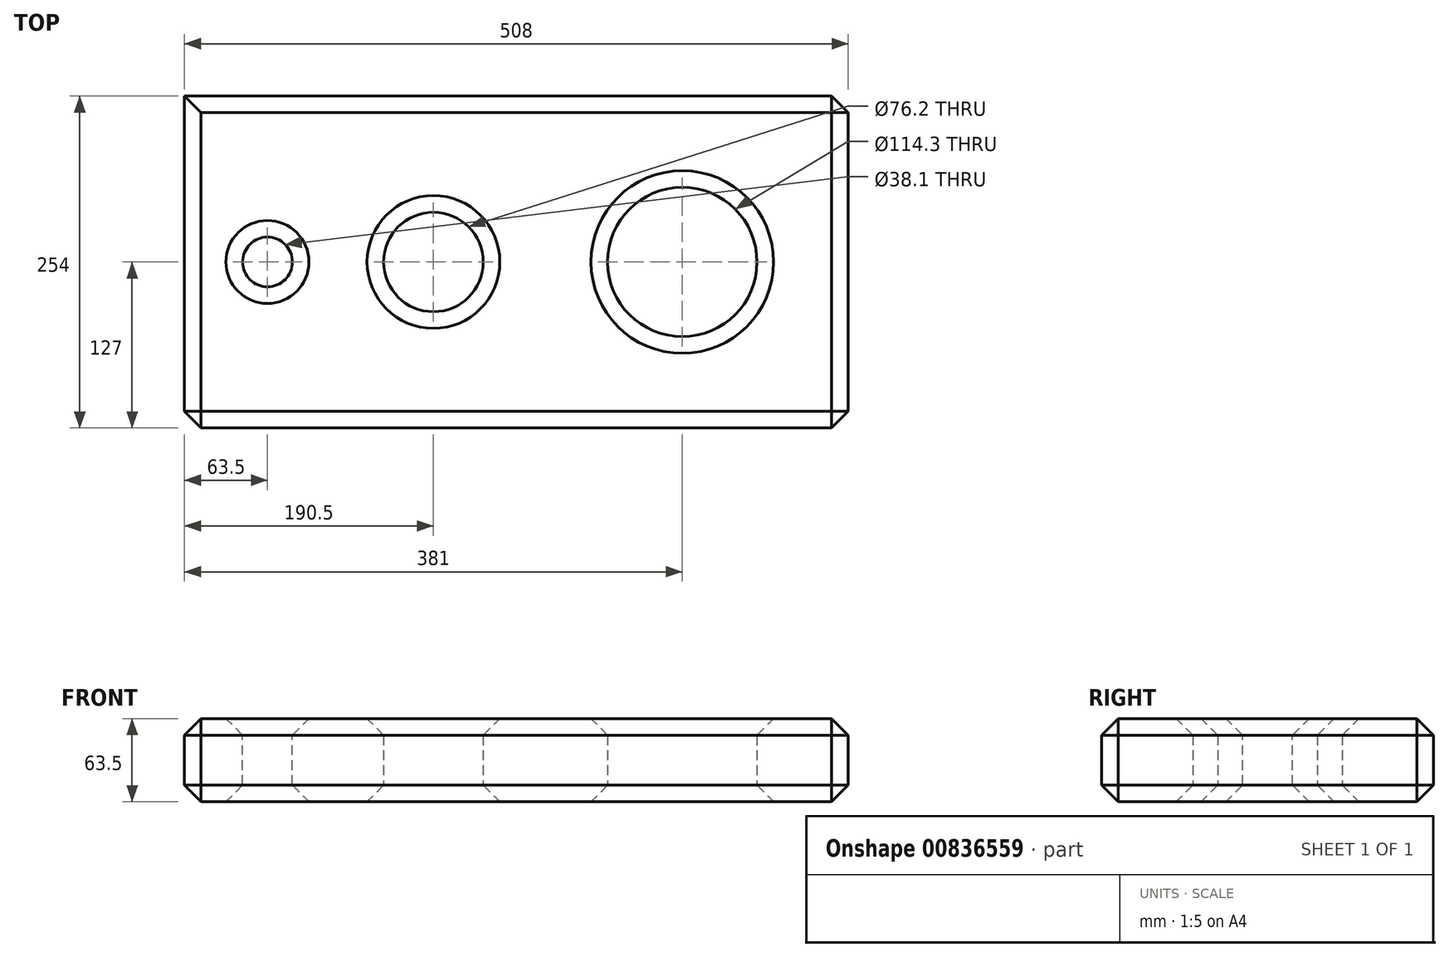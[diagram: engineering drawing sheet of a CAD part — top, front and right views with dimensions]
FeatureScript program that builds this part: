
annotation { "Feature Type Name" : "Feature", "Feature Type Description" : "" }
export const myFeature = defineFeature(function(context is Context, id is Id, definition is map)
    precondition{}
    {
        {
            var Q0;
            Q0=qCreatedBy(makeId("Top.planeOp"),FACE);
            var sketch = newSketch(context, id + "F0", { "sketchPlane" : qUnion([Q0])});
            skLineSegment(sketch, "E0.bottom", {"start": v(-254, 0) * mm, "end": v(254, 0) * mm});
            skLineSegment(sketch, "E0.top", {"start": v(-254, -254) * mm, "end": v(254, -254) * mm});
            skLineSegment(sketch, "E0.left", {"start": v(-254, 0) * mm, "end": v(-254, -254) * mm});
            skLineSegment(sketch, "E0.right", {"start": v(254, 0) * mm, "end": v(254, -254) * mm});
            skSolve(sketch);
        }
        {
            var Q0;
            Q0=makeQuery(id+"F0.imprint","IMPRINT",FACE,{"disambiguationData":[TD([[makeQuery(id+"F0.imprint","IMPRINT",EDGE,{"derivedFrom":sQuery(id+"F0.wireOp",EDGE,"E0.bottom")}),-1.0]])]});
            var sketch = newSketch(context, id + "F1", { "sketchPlane" : qUnion([Q0])});
            skSolve(sketch);
        }
        {
            var Q0;
            Q0 = qSketchRegion(id + "F1", true);
            var Q1;
            Q1=makeQuery(id+"F1.imprint","IMPRINT",FACE,{"disambiguationData":[TD([[makeQuery(id+"F1.imprint","IMPRINT",EDGE,{"derivedFrom":makeQuery(id+"F0.imprint","IMPRINT",EDGE,{"derivedFrom":sQuery(id+"F0.wireOp",EDGE,"E0.bottom")})}),-1.0]])]});
            extrude(context, id + "F2", {"entities" : qUnion([Q0, Q1]), "depth" : 63.5 * mm, "offsetDistance" : 25.4 * mm});
        }
        {
            var Q0;
            Q0=makeQuery(id+"F2.opExtrude","CAP_FACE",FACE,{"disambiguationData":[OSD([sQuery(id+"F0.wireOp",EDGE,"E0.bottom"),sQuery(id+"F0.wireOp",EDGE,"E0.top"),sQuery(id+"F0.wireOp",EDGE,"E0.left"),sQuery(id+"F0.wireOp",EDGE,"E0.right")])],"isStart":false});
            var sketch = newSketch(context, id + "F3", { "sketchPlane" : qUnion([Q0])});
            skCircle(sketch, "E1", {"center": v(-190.5, -127) * mm, "radius": 19.05 * mm});
            skLineSegment(sketch, "E2", {"start": v(-254, -254) * mm, "end": v(-254, 0) * mm});
            skCircle(sketch, "E3", {"center": v(-63.5, -127) * mm, "radius": 38.1 * mm});
            skCircle(sketch, "E4", {"center": v(127, -127) * mm, "radius": 57.15 * mm});
            skSolve(sketch);
        }
        {
            var Q0;
            Q0=makeQuery(id+"F3.imprint","IMPRINT",FACE,{"disambiguationData":[TD([[makeQuery(id+"F3.imprint","IMPRINT",EDGE,{"derivedFrom":sQuery(id+"F3.wireOp",EDGE,"E1")}),-1.0]])]});
            var sketch = newSketch(context, id + "F4", { "sketchPlane" : qUnion([Q0])});
            skSolve(sketch);
        }
        {
            var Q0;
            Q0=makeQuery(id+"F4.imprint","IMPRINT",FACE,{"disambiguationData":[TD([[makeQuery(id+"F4.imprint","IMPRINT",EDGE,{"derivedFrom":makeQuery(id+"F3.imprint","IMPRINT",EDGE,{"derivedFrom":sQuery(id+"F3.wireOp",EDGE,"E3")})}),1.0]])]});
            extrude(context, id + "F5", {"entities" : qUnion([Q0]), "operationType" : NewBodyOperationType.REMOVE, "depth" : 127 * mm, "offsetDistance" : 25.4 * mm, "hasSecondDirection" : true, "secondDirectionOppositeDirection" : true, "secondDirectionDepth" : 127 * mm});
        }
        {
            var Q0;
            Q0=makeQuery(id+"F2.opExtrude","CAP_FACE",FACE,{"disambiguationData":[OSD([sQuery(id+"F0.wireOp",EDGE,"E0.bottom"),sQuery(id+"F0.wireOp",EDGE,"E0.top"),sQuery(id+"F0.wireOp",EDGE,"E0.left"),sQuery(id+"F0.wireOp",EDGE,"E0.right")])],"isStart":false});
            var sketch = newSketch(context, id + "F6", { "sketchPlane" : qUnion([Q0])});
            skLineSegment(sketch, "E5.0", {"start": v(247.65, -6.35) * mm, "end": v(-247.65, -6.35) * mm});
            skLineSegment(sketch, "E5.1", {"start": v(247.65, -247.65) * mm, "end": v(247.65, -6.35) * mm});
            skLineSegment(sketch, "E5.2", {"start": v(-247.65, -247.65) * mm, "end": v(247.65, -247.65) * mm});
            skLineSegment(sketch, "E5.3", {"start": v(-247.65, -6.35) * mm, "end": v(-247.65, -247.65) * mm});
            skCircle(sketch, "E6", {"center": v(127, -127) * mm, "radius": 57.15 * mm});
            skSolve(sketch);
        }
        {
            var Q0;
            Q0=makeQuery(id+"F6.imprint","IMPRINT",FACE,{"disambiguationData":[TD([[makeQuery(id+"F6.imprint","IMPRINT",EDGE,{"derivedFrom":sQuery(id+"F6.wireOp",EDGE,"E6")}),1.0]])]});
            extrude(context, id + "F7", {"entities" : qUnion([Q0]), "operationType" : NewBodyOperationType.REMOVE, "depth" : 127 * mm, "offsetDistance" : 25.4 * mm, "hasSecondDirection" : true, "secondDirectionOppositeDirection" : true, "secondDirectionDepth" : 127 * mm});
        }
        {
            var Q0;
            Q0=makeQuery(id+"F3.imprint","IMPRINT",FACE,{"disambiguationData":[TD([[makeQuery(id+"F3.imprint","IMPRINT",EDGE,{"derivedFrom":sQuery(id+"F3.wireOp",EDGE,"E1")}),1.0]])]});
            extrude(context, id + "F8", {"entities" : qUnion([Q0]), "operationType" : NewBodyOperationType.REMOVE, "oppositeDirection" : true, "depth" : 127 * mm, "offsetDistance" : 25.4 * mm});
        }
        {
            var Q0;
            Q0=makeQuery(id+"F2.opExtrude","CAP_EDGE",EDGE,{"disambiguationData":[OSD([sQuery(id+"F0.wireOp",EDGE,"E0.left")])],"isStart":true});
            var Q1;
            Q1=makeQuery(id+"F2.opExtrude","CAP_EDGE",EDGE,{"disambiguationData":[OSD([sQuery(id+"F0.wireOp",EDGE,"E0.bottom")])],"isStart":true});
            var Q2;
            Q2=makeQuery(id+"F2.opExtrude","SWEPT_FACE",FACE,{"disambiguationData":[OSD([sQuery(id+"F0.wireOp",EDGE,"E0.top")])]});
            var Q3;
            Q3=makeQuery(id+"F2.opExtrude","SWEPT_FACE",FACE,{"disambiguationData":[OSD([sQuery(id+"F0.wireOp",EDGE,"E0.right")])]});
            var Q4;
            Q4=makeQuery(id+"F2.opExtrude","CAP_FACE",FACE,{"disambiguationData":[OSD([sQuery(id+"F0.wireOp",EDGE,"E0.bottom"),sQuery(id+"F0.wireOp",EDGE,"E0.top"),sQuery(id+"F0.wireOp",EDGE,"E0.left"),sQuery(id+"F0.wireOp",EDGE,"E0.right")])],"isStart":false});
            var Q5;
            Q5=makeQuery(id+"F2.opExtrude","SWEPT_EDGE",EDGE,{"disambiguationData":[OSD([sQuery(id+"F0.wireOp",EDGE,"E0.top"),sQuery(id+"F0.wireOp",EDGE,"E0.left")])]});
            var Q6;
            Q6=makeQuery(id+"F8.boolean.opBoolean","INTERSECT",EDGE,{"derivedFrom":[makeQuery(id+"F2.opExtrude","CAP_FACE",FACE,{"disambiguationData":[OSD([sQuery(id+"F0.wireOp",EDGE,"E0.bottom"),sQuery(id+"F0.wireOp",EDGE,"E0.top"),sQuery(id+"F0.wireOp",EDGE,"E0.left"),sQuery(id+"F0.wireOp",EDGE,"E0.right")])],"isStart":true}),makeQuery(id+"F8.opExtrude","SWEPT_FACE",FACE,{"disambiguationData":[OSD([sQuery(id+"F3.wireOp",EDGE,"E1")])]})]});
            var Q7;
            Q7=makeQuery(id+"F5.boolean.opBoolean","INTERSECT",EDGE,{"derivedFrom":[makeQuery(id+"F2.opExtrude","CAP_FACE",FACE,{"disambiguationData":[OSD([sQuery(id+"F0.wireOp",EDGE,"E0.bottom"),sQuery(id+"F0.wireOp",EDGE,"E0.top"),sQuery(id+"F0.wireOp",EDGE,"E0.left"),sQuery(id+"F0.wireOp",EDGE,"E0.right")])],"isStart":true}),makeQuery(id+"F5.opExtrude","SWEPT_FACE",FACE,{"disambiguationData":[OSD([sQuery(id+"F3.wireOp",EDGE,"E3")])]})]});
            var Q8;
            Q8=makeQuery(id+"F7.boolean.opBoolean","INTERSECT",EDGE,{"derivedFrom":[makeQuery(id+"F2.opExtrude","CAP_FACE",FACE,{"disambiguationData":[OSD([sQuery(id+"F0.wireOp",EDGE,"E0.bottom"),sQuery(id+"F0.wireOp",EDGE,"E0.top"),sQuery(id+"F0.wireOp",EDGE,"E0.left"),sQuery(id+"F0.wireOp",EDGE,"E0.right")])],"isStart":true}),makeQuery(id+"F7.opExtrude","SWEPT_FACE",FACE,{"disambiguationData":[OSD([sQuery(id+"F6.wireOp",EDGE,"E6")])]})]});
            chamfer(context, id + "F9", {"entities" : qUnion([Q0, Q1, Q2, Q3, Q4, Q5, Q6, Q7, Q8]), "chamferType" : ChamferType.OFFSET_ANGLE, "width" : 12.7 * mm, "oppositeDirection" : false, "angle" : 45 * degree, "tangentPropagation" : true});
        }
    });
